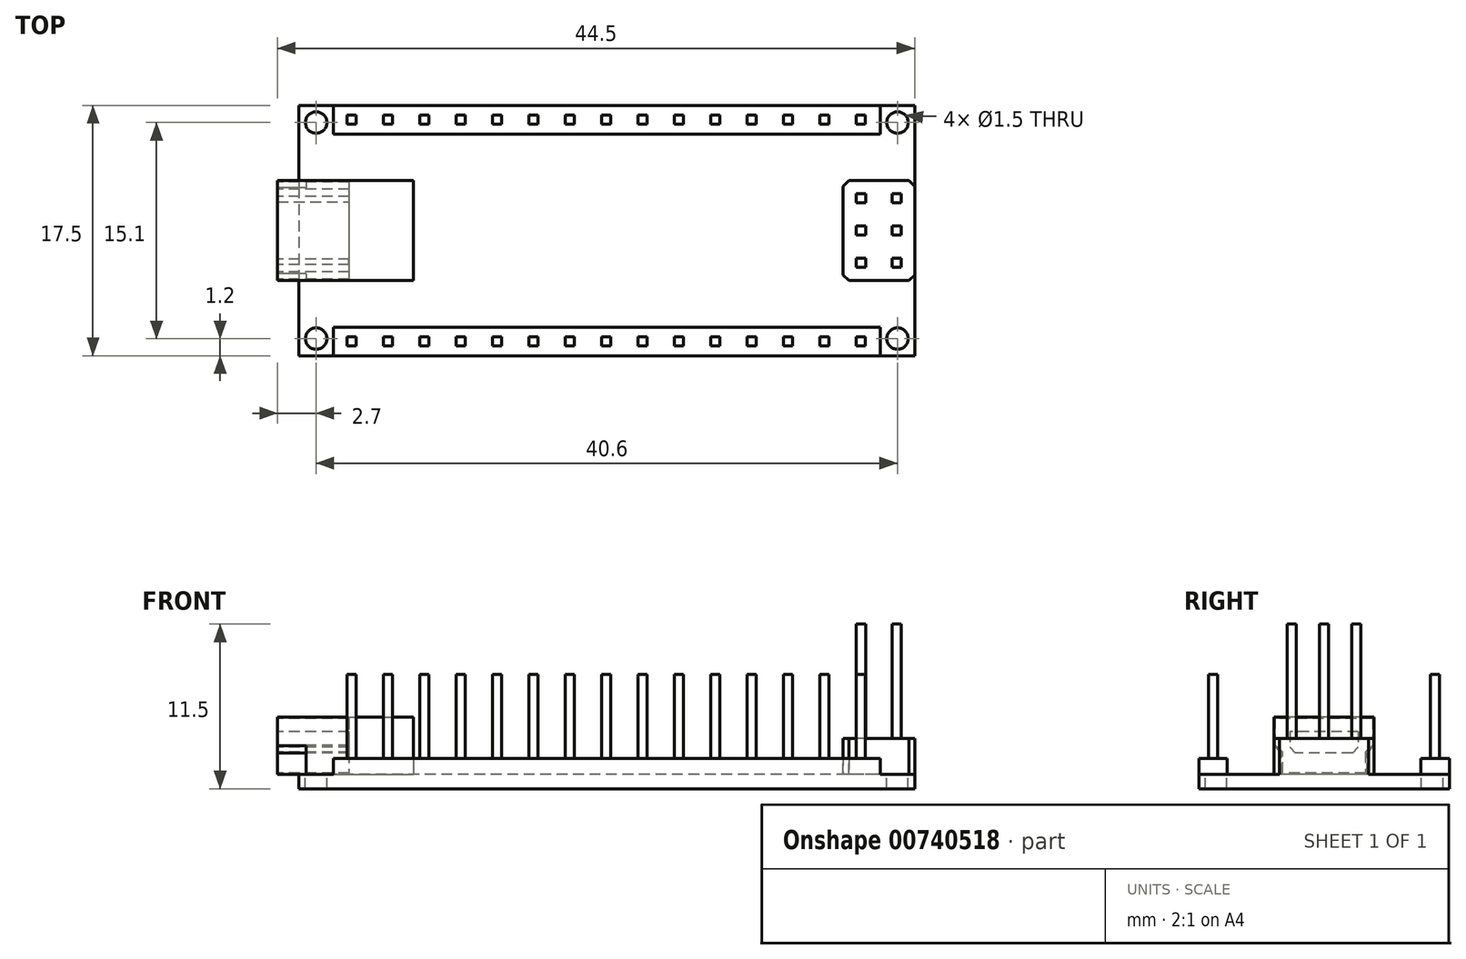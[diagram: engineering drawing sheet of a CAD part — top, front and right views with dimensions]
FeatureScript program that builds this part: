
annotation { "Feature Type Name" : "Feature", "Feature Type Description" : "" }
export const myFeature = defineFeature(function(context is Context, id is Id, definition is map)
    precondition{}
    {
        {
            var Q0;
            Q0=qCreatedBy(makeId("Top.planeOp"),FACE);
            var sketch = newSketch(context, id + "F0", { "sketchPlane" : qUnion([Q0])});
            skLineSegment(sketch, "E0.bottom", {"start": v(21.5, 8.75) * mm, "end": v(-21.5, 8.75) * mm});
            skLineSegment(sketch, "E0.top", {"start": v(21.5, -8.75) * mm, "end": v(-21.5, -8.75) * mm});
            skLineSegment(sketch, "E0.left", {"start": v(21.5, 8.75) * mm, "end": v(21.5, -8.75) * mm});
            skLineSegment(sketch, "E0.right", {"start": v(-21.5, 8.75) * mm, "end": v(-21.5, -8.75) * mm});
            skPoint(sketch, "E0.middle", {"position": v(0, 0) * mm});
            skCircle(sketch, "E1", {"center": v(-20.3, 7.55) * mm, "radius": 0.75 * mm});
            skCircle(sketch, "E2.0.1.0", {"center": v(-20.3, -7.55) * mm, "radius": 0.75 * mm});
            skCircle(sketch, "E2.1.0.0", {"center": v(20.3, 7.55) * mm, "radius": 0.75 * mm});
            skCircle(sketch, "E2.1.1.0", {"center": v(20.3, -7.55) * mm, "radius": 0.75 * mm});
            skLineSegment(sketch, "E2.direction1", {"start": v(-20.3, 7.55) * mm, "end": v(20.3, 7.55) * mm, "construction": true});
            skLineSegment(sketch, "E2.direction2", {"start": v(-20.3, 7.55) * mm, "end": v(-20.3, -7.55) * mm, "construction": true});
            skPoint(sketch, "E3", {"position": v(21.5, 0) * mm});
            skPoint(sketch, "E4", {"position": v(-21.5, 0) * mm});
            skLineSegment(sketch, "E5.bottom", {"start": v(-23, 3.5) * mm, "end": v(-13.5, 3.5) * mm});
            skLineSegment(sketch, "E5.top", {"start": v(-23, -3.5) * mm, "end": v(-13.5, -3.5) * mm});
            skLineSegment(sketch, "E5.left", {"start": v(-23, 3.5) * mm, "end": v(-23, -3.5) * mm});
            skLineSegment(sketch, "E5.right", {"start": v(-13.5, 3.5) * mm, "end": v(-13.5, -3.5) * mm});
            skPoint(sketch, "E6", {"position": v(-13.5, 0) * mm});
            skLineSegment(sketch, "E7.bottom", {"start": v(21.5, 3.5) * mm, "end": v(16.5, 3.5) * mm});
            skLineSegment(sketch, "E7.top", {"start": v(21.5, -3.5) * mm, "end": v(16.5, -3.5) * mm});
            skLineSegment(sketch, "E7.left", {"start": v(21.5, 3.5) * mm, "end": v(21.5, -3.5) * mm});
            skLineSegment(sketch, "E7.right", {"start": v(16.5, 3.5) * mm, "end": v(16.5, -3.5) * mm});
            skSolve(sketch);
        }
        {
            var Q0;
            {var subQ5=sQuery(id+"F0.wireOp",EDGE,"E5.right");Q0=makeQuery(id+"F0.imprint","IMPRINT",FACE,{"disambiguationData":[TD([[makeQuery(id+"F0.imprint","IMPRINT",EDGE,{"derivedFrom":subQ5}),-1.0]])]});}
            var Q1;
            {var subQ1=sQuery(id+"F0.wireOp",EDGE,"E0.bottom");Q1=makeQuery(id+"F0.imprint","IMPRINT",FACE,{"disambiguationData":[TD([[makeQuery(id+"F0.imprint","IMPRINT",EDGE,{"derivedFrom":subQ1}),1.0]])]});}
            var Q2;
            {var subQ0=sQuery(id+"F0.wireOp",EDGE,"E7.bottom");Q2=makeQuery(id+"F0.imprint","IMPRINT",FACE,{"disambiguationData":[TD([[makeQuery(id+"F0.imprint","IMPRINT",EDGE,{"derivedFrom":subQ0}),1.0]])]});}
            extrude(context, id + "F1", {"entities" : qUnion([Q0, Q1, Q2]), "oppositeDirection" : true, "depth" : 1 * mm});
        }
        {
            var Q0;
            {var subQ5=sQuery(id+"F0.wireOp",EDGE,"E5.left");Q0=makeQuery(id+"F0.imprint","IMPRINT",FACE,{"disambiguationData":[TD([[makeQuery(id+"F0.imprint","IMPRINT",EDGE,{"derivedFrom":subQ5}),1.0]])]});}
            var Q1;
            {var subQ5=sQuery(id+"F0.wireOp",EDGE,"E5.right");Q1=makeQuery(id+"F0.imprint","IMPRINT",FACE,{"disambiguationData":[TD([[makeQuery(id+"F0.imprint","IMPRINT",EDGE,{"derivedFrom":subQ5}),-1.0]])]});}
            extrude(context, id + "F2", {"entities" : qUnion([Q0, Q1]), "operationType" : NewBodyOperationType.ADD, "depth" : 4 * mm});
        }
        {
            var Q0;
            {var subQ0=sQuery(id+"F0.wireOp",EDGE,"E7.bottom");Q0=makeQuery(id+"F0.imprint","IMPRINT",FACE,{"disambiguationData":[TD([[makeQuery(id+"F0.imprint","IMPRINT",EDGE,{"derivedFrom":subQ0}),1.0]])]});}
            extrude(context, id + "F3", {"entities" : qUnion([Q0]), "operationType" : NewBodyOperationType.ADD, "depth" : 2.5 * mm});
        }
        {
            var Q0;
            Q0=makeQuery(id+"F2.opExtrude","SWEPT_FACE",FACE,{"disambiguationData":[OSD([sQuery(id+"F0.wireOp",EDGE,"E5.left")])]});
            var sketch = newSketch(context, id + "F4", { "sketchPlane" : qUnion([Q0])});
            skPoint(sketch, "E8", {"position": v(-3.5, 2) * mm});
            skPoint(sketch, "E9", {"position": v(3.5, 2) * mm});
            skPoint(sketch, "E10", {"position": v(-3, 0) * mm});
            skPoint(sketch, "E11", {"position": v(3, 0) * mm});
            skPoint(sketch, "E12", {"position": v(-3, 1.5) * mm});
            skPoint(sketch, "E13", {"position": v(3, 1.5) * mm});
            skLineSegment(sketch, "E14", {"start": v(-3.5, 2) * mm, "end": v(-3, 1.5) * mm});
            skLineSegment(sketch, "E15", {"start": v(-3, 0) * mm, "end": v(-3, 1.5) * mm});
            skLineSegment(sketch, "E16", {"start": v(3, 0) * mm, "end": v(3, 1.5) * mm});
            skLineSegment(sketch, "E17", {"start": v(3, 1.5) * mm, "end": v(3.5, 2) * mm});
            skLineSegment(sketch, "E18.bottom", {"start": v(-2.4, 3) * mm, "end": v(2.4, 3) * mm});
            skLineSegment(sketch, "E18.top", {"start": v(-2.4, 1.5) * mm, "end": v(2.4, 1.5) * mm});
            skLineSegment(sketch, "E18.left", {"start": v(-2.4, 3) * mm, "end": v(-2.4, 1.5) * mm});
            skLineSegment(sketch, "E18.right", {"start": v(2.4, 3) * mm, "end": v(2.4, 1.5) * mm});
            skPoint(sketch, "E19", {"position": v(0, 3) * mm});
            skPoint(sketch, "E20", {"position": v(-2.4, 2.25) * mm});
            skPoint(sketch, "E21", {"position": v(-3.5, 4) * mm});
            skPoint(sketch, "E22", {"position": v(3.5, 4) * mm});
            skLineSegment(sketch, "E23.0", {"start": v(-3.5, -1) * mm, "end": v(3.5, -1) * mm});
            skLineSegment(sketch, "E24", {"start": v(-3.5, 4) * mm, "end": v(-3.5, 2) * mm});
            skLineSegment(sketch, "E25", {"start": v(-3, 1.5) * mm, "end": v(-3, 0) * mm});
            skLineSegment(sketch, "E26", {"start": v(-3, 0) * mm, "end": v(3, 0) * mm});
            skLineSegment(sketch, "E27", {"start": v(3.5, 2) * mm, "end": v(3.5, 4) * mm});
            skLineSegment(sketch, "E28.0", {"start": v(-3.4, 3.9) * mm, "end": v(3.4, 3.9) * mm});
            skLineSegment(sketch, "E28.1", {"start": v(3.4, 2.04) * mm, "end": v(3.4, 3.9) * mm});
            skLineSegment(sketch, "E28.2", {"start": v(-3.4, 3.9) * mm, "end": v(-3.4, 2.04) * mm});
            skLineSegment(sketch, "E28.3", {"start": v(2.9, 1.54) * mm, "end": v(3.4, 2.04) * mm});
            skLineSegment(sketch, "E28.4", {"start": v(-3.4, 2.04) * mm, "end": v(-2.9, 1.54) * mm});
            skLineSegment(sketch, "E28.5", {"start": v(-2.9, 1.54) * mm, "end": v(-2.9, 0.1) * mm});
            skLineSegment(sketch, "E28.6", {"start": v(-2.9, 0.1) * mm, "end": v(2.9, 0.1) * mm});
            skLineSegment(sketch, "E28.7", {"start": v(2.9, 0.1) * mm, "end": v(2.9, 1.54) * mm});
            skPoint(sketch, "E29", {"position": v(-3.4, 2.04) * mm});
            skPoint(sketch, "E30", {"position": v(-2.9, 1.54) * mm});
            skSolve(sketch);
        }
        {
            var Q0;
            Q0=makeQuery(id+"F4.imprint","IMPRINT",FACE,{"disambiguationData":[TD([[makeQuery(id+"F4.imprint","IMPRINT",EDGE,{"derivedFrom":sQuery(id+"F4.wireOp",EDGE,"E18.bottom")}),1.0]])]});
            extrude(context, id + "F5", {"entities" : qUnion([Q0]), "operationType" : NewBodyOperationType.REMOVE, "oppositeDirection" : true, "depth" : 5 * mm});
        }
        {
            var Q0;
            {var subQ0=sQuery(id+"F4.wireOp",EDGE,"E14");Q0=makeQuery(id+"F4.imprint","IMPRINT",FACE,{"disambiguationData":[TD([[makeQuery(id+"F4.imprint","IMPRINT",EDGE,{"derivedFrom":subQ0}),-1.0]])]});}
            var Q1;
            {var subQ0=sQuery(id+"F4.wireOp",EDGE,"E16");Q1=makeQuery(id+"F4.imprint","IMPRINT",FACE,{"disambiguationData":[TD([[makeQuery(id+"F4.imprint","IMPRINT",EDGE,{"derivedFrom":subQ0}),-1.0]])]});}
            extrude(context, id + "F6", {"entities" : qUnion([Q0, Q1]), "operationType" : NewBodyOperationType.REMOVE, "oppositeDirection" : true, "depth" : 2 * mm});
        }
        {
            var Q0;
            Q0=makeQuery(id+"F1.opExtrude","CAP_FACE",FACE,{"disambiguationData":[OSD([sQuery(id+"F0.wireOp",EDGE,"E0.bottom"),sQuery(id+"F0.wireOp",EDGE,"E0.top"),sQuery(id+"F0.wireOp",EDGE,"E0.left"),sQuery(id+"F0.wireOp",EDGE,"E0.right"),sQuery(id+"F0.wireOp",EDGE,"E1"),sQuery(id+"F0.wireOp",EDGE,"E2.0.1.0"),sQuery(id+"F0.wireOp",EDGE,"E2.1.0.0"),sQuery(id+"F0.wireOp",EDGE,"E2.1.1.0")])],"isStart":false});
            var sketch = newSketch(context, id + "F7", { "sketchPlane" : qUnion([Q0])});
            skLineSegment(sketch, "E31.bottom", {"start": v(-19.1, 8.75) * mm, "end": v(19.1, 8.75) * mm});
            skLineSegment(sketch, "E31.top", {"start": v(-19.1, 6.75) * mm, "end": v(19.1, 6.75) * mm});
            skLineSegment(sketch, "E31.left", {"start": v(-19.1, 8.75) * mm, "end": v(-19.1, 6.75) * mm});
            skLineSegment(sketch, "E31.right", {"start": v(19.1, 8.75) * mm, "end": v(19.1, 6.75) * mm});
            skPoint(sketch, "E32", {"position": v(0, 6.75) * mm});
            skLineSegment(sketch, "E33", {"start": v(-19.1, 7.75) * mm, "end": v(19.1, 7.75) * mm, "construction": true});
            skPoint(sketch, "E34", {"position": v(-17.83, 7.75) * mm});
            skLineSegment(sketch, "E35.bottom", {"start": v(-17.51, 8.07) * mm, "end": v(-18.15, 8.07) * mm});
            skLineSegment(sketch, "E35.top", {"start": v(-17.51, 7.43) * mm, "end": v(-18.15, 7.43) * mm});
            skLineSegment(sketch, "E35.left", {"start": v(-17.51, 8.07) * mm, "end": v(-17.51, 7.43) * mm});
            skLineSegment(sketch, "E35.right", {"start": v(-18.15, 8.07) * mm, "end": v(-18.15, 7.43) * mm});
            skPoint(sketch, "E36.1.0.0", {"position": v(-15.3, 7.75) * mm});
            skLineSegment(sketch, "E36.1.0.1", {"start": v(-14.97, 8.07) * mm, "end": v(-14.97, 7.43) * mm});
            skLineSegment(sketch, "E36.1.0.2", {"start": v(-14.97, 8.07) * mm, "end": v(-15.61, 8.07) * mm});
            skLineSegment(sketch, "E36.1.0.3", {"start": v(-15.61, 8.07) * mm, "end": v(-15.61, 7.43) * mm});
            skLineSegment(sketch, "E36.1.0.4", {"start": v(-14.97, 7.43) * mm, "end": v(-15.61, 7.43) * mm});
            skPoint(sketch, "E36.2.0.0", {"position": v(-12.75, 7.75) * mm});
            skLineSegment(sketch, "E36.2.0.1", {"start": v(-12.43, 8.07) * mm, "end": v(-12.43, 7.43) * mm});
            skLineSegment(sketch, "E36.2.0.2", {"start": v(-12.43, 8.07) * mm, "end": v(-13.07, 8.07) * mm});
            skLineSegment(sketch, "E36.2.0.3", {"start": v(-13.07, 8.07) * mm, "end": v(-13.07, 7.43) * mm});
            skLineSegment(sketch, "E36.2.0.4", {"start": v(-12.43, 7.43) * mm, "end": v(-13.07, 7.43) * mm});
            skPoint(sketch, "E36.3.0.0", {"position": v(-10.21, 7.75) * mm});
            skLineSegment(sketch, "E36.3.0.1", {"start": v(-9.89, 8.07) * mm, "end": v(-9.89, 7.43) * mm});
            skLineSegment(sketch, "E36.3.0.2", {"start": v(-9.89, 8.07) * mm, "end": v(-10.53, 8.07) * mm});
            skLineSegment(sketch, "E36.3.0.3", {"start": v(-10.53, 8.07) * mm, "end": v(-10.53, 7.43) * mm});
            skLineSegment(sketch, "E36.3.0.4", {"start": v(-9.89, 7.43) * mm, "end": v(-10.53, 7.43) * mm});
            skPoint(sketch, "E36.4.0.0", {"position": v(-7.67, 7.75) * mm});
            skLineSegment(sketch, "E36.4.0.1", {"start": v(-7.35, 8.07) * mm, "end": v(-7.35, 7.43) * mm});
            skLineSegment(sketch, "E36.4.0.2", {"start": v(-7.35, 8.07) * mm, "end": v(-8, 8.07) * mm});
            skLineSegment(sketch, "E36.4.0.3", {"start": v(-8, 8.07) * mm, "end": v(-8, 7.43) * mm});
            skLineSegment(sketch, "E36.4.0.4", {"start": v(-7.35, 7.43) * mm, "end": v(-8, 7.43) * mm});
            skPoint(sketch, "E36.5.0.0", {"position": v(-5.13, 7.75) * mm});
            skLineSegment(sketch, "E36.5.0.1", {"start": v(-4.8, 8.07) * mm, "end": v(-4.8, 7.43) * mm});
            skLineSegment(sketch, "E36.5.0.2", {"start": v(-4.8, 8.07) * mm, "end": v(-5.45, 8.07) * mm});
            skLineSegment(sketch, "E36.5.0.3", {"start": v(-5.45, 8.07) * mm, "end": v(-5.45, 7.43) * mm});
            skLineSegment(sketch, "E36.5.0.4", {"start": v(-4.8, 7.43) * mm, "end": v(-5.45, 7.43) * mm});
            skPoint(sketch, "E36.6.0.0", {"position": v(-2.59, 7.75) * mm});
            skLineSegment(sketch, "E36.6.0.1", {"start": v(-2.27, 8.07) * mm, "end": v(-2.27, 7.43) * mm});
            skLineSegment(sketch, "E36.6.0.2", {"start": v(-2.27, 8.07) * mm, "end": v(-2.9, 8.07) * mm});
            skLineSegment(sketch, "E36.6.0.3", {"start": v(-2.9, 8.07) * mm, "end": v(-2.9, 7.43) * mm});
            skLineSegment(sketch, "E36.6.0.4", {"start": v(-2.27, 7.43) * mm, "end": v(-2.9, 7.43) * mm});
            skPoint(sketch, "E36.7.0.0", {"position": v(-0.05, 7.75) * mm});
            skLineSegment(sketch, "E36.7.0.1", {"start": v(0.27, 8.07) * mm, "end": v(0.27, 7.43) * mm});
            skLineSegment(sketch, "E36.7.0.2", {"start": v(0.27, 8.07) * mm, "end": v(-0.37, 8.07) * mm});
            skLineSegment(sketch, "E36.7.0.3", {"start": v(-0.37, 8.07) * mm, "end": v(-0.37, 7.43) * mm});
            skLineSegment(sketch, "E36.7.0.4", {"start": v(0.27, 7.43) * mm, "end": v(-0.37, 7.43) * mm});
            skPoint(sketch, "E36.8.0.0", {"position": v(2.5, 7.75) * mm});
            skLineSegment(sketch, "E36.8.0.1", {"start": v(2.81, 8.07) * mm, "end": v(2.81, 7.43) * mm});
            skLineSegment(sketch, "E36.8.0.2", {"start": v(2.81, 8.07) * mm, "end": v(2.17, 8.07) * mm});
            skLineSegment(sketch, "E36.8.0.3", {"start": v(2.17, 8.07) * mm, "end": v(2.17, 7.43) * mm});
            skLineSegment(sketch, "E36.8.0.4", {"start": v(2.81, 7.43) * mm, "end": v(2.17, 7.43) * mm});
            skPoint(sketch, "E36.9.0.0", {"position": v(5.03, 7.75) * mm});
            skLineSegment(sketch, "E36.9.0.1", {"start": v(5.35, 8.07) * mm, "end": v(5.35, 7.43) * mm});
            skLineSegment(sketch, "E36.9.0.2", {"start": v(5.35, 8.07) * mm, "end": v(4.71, 8.07) * mm});
            skLineSegment(sketch, "E36.9.0.3", {"start": v(4.71, 8.07) * mm, "end": v(4.71, 7.43) * mm});
            skLineSegment(sketch, "E36.9.0.4", {"start": v(5.35, 7.43) * mm, "end": v(4.71, 7.43) * mm});
            skPoint(sketch, "E36.10.0.0", {"position": v(7.57, 7.75) * mm});
            skLineSegment(sketch, "E36.10.0.1", {"start": v(7.9, 8.07) * mm, "end": v(7.9, 7.43) * mm});
            skLineSegment(sketch, "E36.10.0.2", {"start": v(7.9, 8.07) * mm, "end": v(7.25, 8.07) * mm});
            skLineSegment(sketch, "E36.10.0.3", {"start": v(7.25, 8.07) * mm, "end": v(7.25, 7.43) * mm});
            skLineSegment(sketch, "E36.10.0.4", {"start": v(7.9, 7.43) * mm, "end": v(7.25, 7.43) * mm});
            skPoint(sketch, "E36.11.0.0", {"position": v(10.11, 7.75) * mm});
            skLineSegment(sketch, "E36.11.0.1", {"start": v(10.43, 8.07) * mm, "end": v(10.43, 7.43) * mm});
            skLineSegment(sketch, "E36.11.0.2", {"start": v(10.43, 8.07) * mm, "end": v(9.8, 8.07) * mm});
            skLineSegment(sketch, "E36.11.0.3", {"start": v(9.8, 8.07) * mm, "end": v(9.8, 7.43) * mm});
            skLineSegment(sketch, "E36.11.0.4", {"start": v(10.43, 7.43) * mm, "end": v(9.8, 7.43) * mm});
            skPoint(sketch, "E36.12.0.0", {"position": v(12.65, 7.75) * mm});
            skLineSegment(sketch, "E36.12.0.1", {"start": v(12.97, 8.07) * mm, "end": v(12.97, 7.43) * mm});
            skLineSegment(sketch, "E36.12.0.2", {"start": v(12.97, 8.07) * mm, "end": v(12.33, 8.07) * mm});
            skLineSegment(sketch, "E36.12.0.3", {"start": v(12.33, 8.07) * mm, "end": v(12.33, 7.43) * mm});
            skLineSegment(sketch, "E36.12.0.4", {"start": v(12.97, 7.43) * mm, "end": v(12.33, 7.43) * mm});
            skPoint(sketch, "E36.13.0.0", {"position": v(15.2, 7.75) * mm});
            skLineSegment(sketch, "E36.13.0.1", {"start": v(15.51, 8.07) * mm, "end": v(15.51, 7.43) * mm});
            skLineSegment(sketch, "E36.13.0.2", {"start": v(15.51, 8.07) * mm, "end": v(14.87, 8.07) * mm});
            skLineSegment(sketch, "E36.13.0.3", {"start": v(14.87, 8.07) * mm, "end": v(14.87, 7.43) * mm});
            skLineSegment(sketch, "E36.13.0.4", {"start": v(15.51, 7.43) * mm, "end": v(14.87, 7.43) * mm});
            skPoint(sketch, "E36.14.0.0", {"position": v(17.73, 7.75) * mm});
            skLineSegment(sketch, "E36.14.0.1", {"start": v(18.05, 8.07) * mm, "end": v(18.05, 7.43) * mm});
            skLineSegment(sketch, "E36.14.0.2", {"start": v(18.05, 8.07) * mm, "end": v(17.41, 8.07) * mm});
            skLineSegment(sketch, "E36.14.0.3", {"start": v(17.41, 8.07) * mm, "end": v(17.41, 7.43) * mm});
            skLineSegment(sketch, "E36.14.0.4", {"start": v(18.05, 7.43) * mm, "end": v(17.41, 7.43) * mm});
            skLineSegment(sketch, "E36.direction1", {"start": v(-17.83, 7.75) * mm, "end": v(-15.3, 7.75) * mm, "construction": true});
            skPoint(sketch, "E37", {"position": v(-20.3, 7.55) * mm});
            skLineSegment(sketch, "E38", {"start": v(-20.3, 7.55) * mm, "end": v(-21.5, 7.55) * mm});
            skLineSegment(sketch, "E39", {"start": v(-21.5, 7.55) * mm, "end": v(-19.1, 7.55) * mm});
            skPoint(sketch, "E40", {"position": v(-21.05, 7.55) * mm});
            skPoint(sketch, "E41", {"position": v(-19.55, 7.55) * mm});
            skPoint(sketch, "E42", {"position": v(20.3, 7.55) * mm});
            skLineSegment(sketch, "E43", {"start": v(20.3, 7.55) * mm, "end": v(21.5, 7.55) * mm});
            skLineSegment(sketch, "E44", {"start": v(21.5, 7.55) * mm, "end": v(19.1, 7.55) * mm});
            skPoint(sketch, "E45", {"position": v(21.05, 7.55) * mm});
            skPoint(sketch, "E46", {"position": v(19.55, 7.55) * mm});
            skPoint(sketch, "E47.0.1.0", {"position": v(-0.05, -7.75) * mm});
            skPoint(sketch, "E47.0.1.1", {"position": v(-5.13, -7.75) * mm});
            skPoint(sketch, "E47.0.1.2", {"position": v(12.65, -7.75) * mm});
            skPoint(sketch, "E47.0.1.3", {"position": v(-7.67, -7.75) * mm});
            skPoint(sketch, "E47.0.1.4", {"position": v(17.73, -7.75) * mm});
            skPoint(sketch, "E47.0.1.5", {"position": v(-10.21, -7.75) * mm});
            skPoint(sketch, "E47.0.1.6", {"position": v(7.57, -7.75) * mm});
            skPoint(sketch, "E47.0.1.7", {"position": v(2.49, -7.75) * mm});
            skPoint(sketch, "E47.0.1.8", {"position": v(0, -8.75) * mm});
            skPoint(sketch, "E47.0.1.9", {"position": v(-17.83, -7.75) * mm});
            skPoint(sketch, "E47.0.1.10", {"position": v(5.03, -7.75) * mm});
            skPoint(sketch, "E47.0.1.11", {"position": v(-15.3, -7.75) * mm});
            skLineSegment(sketch, "E47.0.1.12", {"start": v(-17.83, -7.75) * mm, "end": v(-15.3, -7.75) * mm, "construction": true});
            skPoint(sketch, "E47.0.1.13", {"position": v(10.11, -7.75) * mm});
            skPoint(sketch, "E47.0.1.14", {"position": v(15.2, -7.75) * mm});
            skPoint(sketch, "E47.0.1.15", {"position": v(-2.6, -7.75) * mm});
            skPoint(sketch, "E47.0.1.16", {"position": v(-12.75, -7.75) * mm});
            skPoint(sketch, "E47.0.1.17", {"position": v(-17.83, -7.75) * mm});
            skLineSegment(sketch, "E47.0.1.18", {"start": v(18.05, -7.43) * mm, "end": v(17.41, -7.43) * mm});
            skLineSegment(sketch, "E47.0.1.19", {"start": v(18.05, -8.07) * mm, "end": v(17.41, -8.07) * mm});
            skLineSegment(sketch, "E47.0.1.20", {"start": v(18.05, -7.43) * mm, "end": v(18.05, -8.07) * mm});
            skLineSegment(sketch, "E47.0.1.21", {"start": v(-0.37, -7.43) * mm, "end": v(-0.37, -8.07) * mm});
            skLineSegment(sketch, "E47.0.1.22", {"start": v(-10.53, -7.43) * mm, "end": v(-10.53, -8.07) * mm});
            skLineSegment(sketch, "E47.0.1.23", {"start": v(-9.89, -7.43) * mm, "end": v(-10.53, -7.43) * mm});
            skLineSegment(sketch, "E47.0.1.24", {"start": v(-2.27, -7.43) * mm, "end": v(-2.9, -7.43) * mm});
            skLineSegment(sketch, "E47.0.1.25", {"start": v(12.97, -7.43) * mm, "end": v(12.97, -8.07) * mm});
            skLineSegment(sketch, "E47.0.1.26", {"start": v(-5.45, -7.43) * mm, "end": v(-5.45, -8.07) * mm});
            skLineSegment(sketch, "E47.0.1.27", {"start": v(-7.35, -8.07) * mm, "end": v(-7.99, -8.07) * mm});
            skLineSegment(sketch, "E47.0.1.28", {"start": v(2.81, -8.07) * mm, "end": v(2.17, -8.07) * mm});
            skLineSegment(sketch, "E47.0.1.29", {"start": v(12.97, -8.07) * mm, "end": v(12.33, -8.07) * mm});
            skLineSegment(sketch, "E47.0.1.30", {"start": v(7.9, -8.07) * mm, "end": v(7.25, -8.07) * mm});
            skLineSegment(sketch, "E47.0.1.31", {"start": v(7.25, -7.43) * mm, "end": v(7.25, -8.07) * mm});
            skLineSegment(sketch, "E47.0.1.32", {"start": v(-2.9, -7.43) * mm, "end": v(-2.9, -8.07) * mm});
            skLineSegment(sketch, "E47.0.1.33", {"start": v(-7.35, -7.43) * mm, "end": v(-7.99, -7.43) * mm});
            skLineSegment(sketch, "E47.0.1.34", {"start": v(2.81, -7.43) * mm, "end": v(2.81, -8.07) * mm});
            skLineSegment(sketch, "E47.0.1.35", {"start": v(7.9, -7.43) * mm, "end": v(7.25, -7.43) * mm});
            skLineSegment(sketch, "E47.0.1.36", {"start": v(-4.8, -8.07) * mm, "end": v(-5.45, -8.07) * mm});
            skLineSegment(sketch, "E47.0.1.37", {"start": v(-7.35, -7.43) * mm, "end": v(-7.35, -8.07) * mm});
            skLineSegment(sketch, "E47.0.1.38", {"start": v(15.5, -8.07) * mm, "end": v(14.87, -8.07) * mm});
            skLineSegment(sketch, "E47.0.1.39", {"start": v(5.35, -8.07) * mm, "end": v(4.71, -8.07) * mm});
            skLineSegment(sketch, "E47.0.1.40", {"start": v(-2.27, -8.07) * mm, "end": v(-2.9, -8.07) * mm});
            skLineSegment(sketch, "E47.0.1.41", {"start": v(-12.43, -8.07) * mm, "end": v(-13.07, -8.07) * mm});
            skLineSegment(sketch, "E47.0.1.42", {"start": v(2.81, -7.43) * mm, "end": v(2.17, -7.43) * mm});
            skLineSegment(sketch, "E47.0.1.43", {"start": v(17.41, -7.43) * mm, "end": v(17.41, -8.07) * mm});
            skLineSegment(sketch, "E47.0.1.44", {"start": v(12.97, -7.43) * mm, "end": v(12.33, -7.43) * mm});
            skLineSegment(sketch, "E47.0.1.45", {"start": v(7.9, -7.43) * mm, "end": v(7.9, -8.07) * mm});
            skLineSegment(sketch, "E47.0.1.46", {"start": v(-2.27, -7.43) * mm, "end": v(-2.27, -8.07) * mm});
            skLineSegment(sketch, "E47.0.1.47", {"start": v(-17.5, -8.07) * mm, "end": v(-18.15, -8.07) * mm});
            skLineSegment(sketch, "E47.0.1.48", {"start": v(12.33, -7.43) * mm, "end": v(12.33, -8.07) * mm});
            skLineSegment(sketch, "E47.0.1.49", {"start": v(-14.97, -7.43) * mm, "end": v(-14.97, -8.07) * mm});
            skLineSegment(sketch, "E47.0.1.50", {"start": v(2.17, -7.43) * mm, "end": v(2.17, -8.07) * mm});
            skLineSegment(sketch, "E47.0.1.51", {"start": v(-8, -7.43) * mm, "end": v(-8, -8.07) * mm});
            skLineSegment(sketch, "E47.0.1.52", {"start": v(-14.97, -7.43) * mm, "end": v(-15.6, -7.43) * mm});
            skLineSegment(sketch, "E47.0.1.53", {"start": v(-15.61, -7.43) * mm, "end": v(-15.61, -8.07) * mm});
            skLineSegment(sketch, "E47.0.1.54", {"start": v(-14.97, -8.07) * mm, "end": v(-15.6, -8.07) * mm});
            skLineSegment(sketch, "E47.0.1.55", {"start": v(-9.89, -7.43) * mm, "end": v(-9.89, -8.07) * mm});
            skLineSegment(sketch, "E47.0.1.56", {"start": v(0.27, -7.43) * mm, "end": v(0.27, -8.07) * mm});
            skLineSegment(sketch, "E47.0.1.57", {"start": v(10.43, -7.43) * mm, "end": v(10.43, -8.07) * mm});
            skLineSegment(sketch, "E47.0.1.58", {"start": v(-12.43, -7.43) * mm, "end": v(-12.43, -8.07) * mm});
            skLineSegment(sketch, "E47.0.1.59", {"start": v(10.43, -7.43) * mm, "end": v(9.8, -7.43) * mm});
            skLineSegment(sketch, "E47.0.1.60", {"start": v(0.27, -7.43) * mm, "end": v(-0.37, -7.43) * mm});
            skLineSegment(sketch, "E47.0.1.61", {"start": v(15.51, -7.43) * mm, "end": v(15.51, -8.07) * mm});
            skLineSegment(sketch, "E47.0.1.62", {"start": v(5.35, -7.43) * mm, "end": v(5.35, -8.07) * mm});
            skLineSegment(sketch, "E47.0.1.63", {"start": v(-4.8, -7.43) * mm, "end": v(-4.8, -8.07) * mm});
            skLineSegment(sketch, "E47.0.1.64", {"start": v(15.51, -7.43) * mm, "end": v(14.87, -7.43) * mm});
            skLineSegment(sketch, "E47.0.1.65", {"start": v(5.35, -7.43) * mm, "end": v(4.71, -7.43) * mm});
            skLineSegment(sketch, "E47.0.1.66", {"start": v(-4.8, -7.43) * mm, "end": v(-5.45, -7.43) * mm});
            skLineSegment(sketch, "E47.0.1.67", {"start": v(10.43, -8.07) * mm, "end": v(9.8, -8.07) * mm});
            skLineSegment(sketch, "E47.0.1.68", {"start": v(0.27, -8.07) * mm, "end": v(-0.37, -8.07) * mm});
            skLineSegment(sketch, "E47.0.1.69", {"start": v(-9.9, -8.07) * mm, "end": v(-10.53, -8.07) * mm});
            skLineSegment(sketch, "E47.0.1.70", {"start": v(4.71, -7.43) * mm, "end": v(4.71, -8.07) * mm});
            skLineSegment(sketch, "E47.0.1.71", {"start": v(14.87, -7.43) * mm, "end": v(14.87, -8.07) * mm});
            skLineSegment(sketch, "E47.0.1.72", {"start": v(9.8, -7.43) * mm, "end": v(9.8, -8.07) * mm});
            skLineSegment(sketch, "E47.0.1.73", {"start": v(-12.43, -7.43) * mm, "end": v(-13.07, -7.43) * mm});
            skLineSegment(sketch, "E47.0.1.74", {"start": v(-13.07, -7.43) * mm, "end": v(-13.07, -8.07) * mm});
            skLineSegment(sketch, "E47.0.1.75", {"start": v(-18.15, -7.43) * mm, "end": v(-18.15, -8.07) * mm});
            skLineSegment(sketch, "E47.0.1.76", {"start": v(-17.51, -7.43) * mm, "end": v(-17.51, -8.07) * mm});
            skLineSegment(sketch, "E47.0.1.77", {"start": v(-17.5, -7.43) * mm, "end": v(-18.15, -7.43) * mm});
            skLineSegment(sketch, "E47.0.1.78", {"start": v(19.1, -6.75) * mm, "end": v(19.1, -8.75) * mm});
            skLineSegment(sketch, "E47.0.1.79", {"start": v(-19.1, -8.75) * mm, "end": v(19.1, -8.75) * mm});
            skLineSegment(sketch, "E47.0.1.80", {"start": v(-19.1, -6.75) * mm, "end": v(-19.1, -8.75) * mm});
            skLineSegment(sketch, "E47.0.1.81", {"start": v(-19.1, -6.75) * mm, "end": v(19.1, -6.75) * mm});
            skLineSegment(sketch, "E47.direction1", {"start": v(-0.05, 7.75) * mm, "end": v(24.95, 7.75) * mm, "construction": true});
            skLineSegment(sketch, "E47.direction2", {"start": v(-0.05, 7.75) * mm, "end": v(-0.05, -7.75) * mm, "construction": true});
            skSolve(sketch);
        }
        {
            var Q0;
            Q0=makeQuery(id+"F7.imprint","IMPRINT",FACE,{"disambiguationData":[TD([[makeQuery(id+"F7.imprint","IMPRINT",EDGE,{"derivedFrom":sQuery(id+"F7.wireOp",EDGE,"E47.0.1.18")}),-1.0]])]});
            var Q1;
            {var subQ1=sQuery(id+"F7.wireOp",EDGE,"E31.bottom");Q1=makeQuery(id+"F7.imprint","IMPRINT",FACE,{"disambiguationData":[TD([[makeQuery(id+"F7.imprint","IMPRINT",EDGE,{"derivedFrom":subQ1}),1.0]])]});}
            extrude(context, id + "F8", {"entities" : qUnion([Q0, Q1]), "oppositeDirection" : true, "depth" : 2.1 * mm, "offsetDistance" : 25 * mm});
        }
        {
            var Q0;
            Q0=makeQuery(id+"F7.imprint","IMPRINT",FACE,{"disambiguationData":[TD([[makeQuery(id+"F7.imprint","IMPRINT",EDGE,{"derivedFrom":sQuery(id+"F7.wireOp",EDGE,"E35.bottom")}),1.0]])]});
            var Q1;
            Q1=makeQuery(id+"F7.imprint","IMPRINT",FACE,{"disambiguationData":[TD([[makeQuery(id+"F7.imprint","IMPRINT",EDGE,{"derivedFrom":sQuery(id+"F7.wireOp",EDGE,"E36.1.0.1")}),-1.0]])]});
            var Q2;
            Q2=makeQuery(id+"F7.imprint","IMPRINT",FACE,{"disambiguationData":[TD([[makeQuery(id+"F7.imprint","IMPRINT",EDGE,{"derivedFrom":sQuery(id+"F7.wireOp",EDGE,"E36.2.0.1")}),-1.0]])]});
            var Q3;
            Q3=makeQuery(id+"F7.imprint","IMPRINT",FACE,{"disambiguationData":[TD([[makeQuery(id+"F7.imprint","IMPRINT",EDGE,{"derivedFrom":sQuery(id+"F7.wireOp",EDGE,"E36.3.0.1")}),-1.0]])]});
            var Q4;
            Q4=makeQuery(id+"F7.imprint","IMPRINT",FACE,{"disambiguationData":[TD([[makeQuery(id+"F7.imprint","IMPRINT",EDGE,{"derivedFrom":sQuery(id+"F7.wireOp",EDGE,"E36.4.0.1")}),-1.0]])]});
            var Q5;
            Q5=makeQuery(id+"F7.imprint","IMPRINT",FACE,{"disambiguationData":[TD([[makeQuery(id+"F7.imprint","IMPRINT",EDGE,{"derivedFrom":sQuery(id+"F7.wireOp",EDGE,"E36.5.0.1")}),-1.0]])]});
            var Q6;
            Q6=makeQuery(id+"F7.imprint","IMPRINT",FACE,{"disambiguationData":[TD([[makeQuery(id+"F7.imprint","IMPRINT",EDGE,{"derivedFrom":sQuery(id+"F7.wireOp",EDGE,"E36.6.0.1")}),-1.0]])]});
            var Q7;
            Q7=makeQuery(id+"F7.imprint","IMPRINT",FACE,{"disambiguationData":[TD([[makeQuery(id+"F7.imprint","IMPRINT",EDGE,{"derivedFrom":sQuery(id+"F7.wireOp",EDGE,"E36.7.0.1")}),-1.0]])]});
            var Q8;
            Q8=makeQuery(id+"F7.imprint","IMPRINT",FACE,{"disambiguationData":[TD([[makeQuery(id+"F7.imprint","IMPRINT",EDGE,{"derivedFrom":sQuery(id+"F7.wireOp",EDGE,"E36.8.0.1")}),-1.0]])]});
            var Q9;
            Q9=makeQuery(id+"F7.imprint","IMPRINT",FACE,{"disambiguationData":[TD([[makeQuery(id+"F7.imprint","IMPRINT",EDGE,{"derivedFrom":sQuery(id+"F7.wireOp",EDGE,"E36.9.0.1")}),-1.0]])]});
            var Q10;
            Q10=makeQuery(id+"F7.imprint","IMPRINT",FACE,{"disambiguationData":[TD([[makeQuery(id+"F7.imprint","IMPRINT",EDGE,{"derivedFrom":sQuery(id+"F7.wireOp",EDGE,"E36.10.0.1")}),-1.0]])]});
            var Q11;
            Q11=makeQuery(id+"F7.imprint","IMPRINT",FACE,{"disambiguationData":[TD([[makeQuery(id+"F7.imprint","IMPRINT",EDGE,{"derivedFrom":sQuery(id+"F7.wireOp",EDGE,"E36.11.0.1")}),-1.0]])]});
            var Q12;
            Q12=makeQuery(id+"F7.imprint","IMPRINT",FACE,{"disambiguationData":[TD([[makeQuery(id+"F7.imprint","IMPRINT",EDGE,{"derivedFrom":sQuery(id+"F7.wireOp",EDGE,"E36.12.0.1")}),-1.0]])]});
            var Q13;
            Q13=makeQuery(id+"F7.imprint","IMPRINT",FACE,{"disambiguationData":[TD([[makeQuery(id+"F7.imprint","IMPRINT",EDGE,{"derivedFrom":sQuery(id+"F7.wireOp",EDGE,"E36.13.0.1")}),-1.0]])]});
            var Q14;
            Q14=makeQuery(id+"F7.imprint","IMPRINT",FACE,{"disambiguationData":[TD([[makeQuery(id+"F7.imprint","IMPRINT",EDGE,{"derivedFrom":sQuery(id+"F7.wireOp",EDGE,"E36.14.0.1")}),-1.0]])]});
            var Q15;
            Q15=makeQuery(id+"F7.imprint","IMPRINT",FACE,{"disambiguationData":[TD([[makeQuery(id+"F7.imprint","IMPRINT",EDGE,{"derivedFrom":sQuery(id+"F7.wireOp",EDGE,"E47.0.1.47")}),-1.0]])]});
            var Q16;
            Q16=makeQuery(id+"F7.imprint","IMPRINT",FACE,{"disambiguationData":[TD([[makeQuery(id+"F7.imprint","IMPRINT",EDGE,{"derivedFrom":sQuery(id+"F7.wireOp",EDGE,"E47.0.1.49")}),-1.0]])]});
            var Q17;
            Q17=makeQuery(id+"F7.imprint","IMPRINT",FACE,{"disambiguationData":[TD([[makeQuery(id+"F7.imprint","IMPRINT",EDGE,{"derivedFrom":sQuery(id+"F7.wireOp",EDGE,"E47.0.1.41")}),-1.0]])]});
            var Q18;
            Q18=makeQuery(id+"F7.imprint","IMPRINT",FACE,{"disambiguationData":[TD([[makeQuery(id+"F7.imprint","IMPRINT",EDGE,{"derivedFrom":sQuery(id+"F7.wireOp",EDGE,"E47.0.1.22")}),1.0]])]});
            var Q19;
            Q19=makeQuery(id+"F7.imprint","IMPRINT",FACE,{"disambiguationData":[TD([[makeQuery(id+"F7.imprint","IMPRINT",EDGE,{"derivedFrom":sQuery(id+"F7.wireOp",EDGE,"E47.0.1.27")}),-1.0]])]});
            var Q20;
            Q20=makeQuery(id+"F7.imprint","IMPRINT",FACE,{"disambiguationData":[TD([[makeQuery(id+"F7.imprint","IMPRINT",EDGE,{"derivedFrom":sQuery(id+"F7.wireOp",EDGE,"E47.0.1.26")}),1.0]])]});
            var Q21;
            Q21=makeQuery(id+"F7.imprint","IMPRINT",FACE,{"disambiguationData":[TD([[makeQuery(id+"F7.imprint","IMPRINT",EDGE,{"derivedFrom":sQuery(id+"F7.wireOp",EDGE,"E47.0.1.24")}),1.0]])]});
            var Q22;
            Q22=makeQuery(id+"F7.imprint","IMPRINT",FACE,{"disambiguationData":[TD([[makeQuery(id+"F7.imprint","IMPRINT",EDGE,{"derivedFrom":sQuery(id+"F7.wireOp",EDGE,"E47.0.1.21")}),1.0]])]});
            var Q23;
            Q23=makeQuery(id+"F7.imprint","IMPRINT",FACE,{"disambiguationData":[TD([[makeQuery(id+"F7.imprint","IMPRINT",EDGE,{"derivedFrom":sQuery(id+"F7.wireOp",EDGE,"E47.0.1.28")}),-1.0]])]});
            var Q24;
            Q24=makeQuery(id+"F7.imprint","IMPRINT",FACE,{"disambiguationData":[TD([[makeQuery(id+"F7.imprint","IMPRINT",EDGE,{"derivedFrom":sQuery(id+"F7.wireOp",EDGE,"E47.0.1.39")}),-1.0]])]});
            var Q25;
            Q25=makeQuery(id+"F7.imprint","IMPRINT",FACE,{"disambiguationData":[TD([[makeQuery(id+"F7.imprint","IMPRINT",EDGE,{"derivedFrom":sQuery(id+"F7.wireOp",EDGE,"E47.0.1.30")}),-1.0]])]});
            var Q26;
            Q26=makeQuery(id+"F7.imprint","IMPRINT",FACE,{"disambiguationData":[TD([[makeQuery(id+"F7.imprint","IMPRINT",EDGE,{"derivedFrom":sQuery(id+"F7.wireOp",EDGE,"E47.0.1.57")}),-1.0]])]});
            var Q27;
            Q27=makeQuery(id+"F7.imprint","IMPRINT",FACE,{"disambiguationData":[TD([[makeQuery(id+"F7.imprint","IMPRINT",EDGE,{"derivedFrom":sQuery(id+"F7.wireOp",EDGE,"E47.0.1.25")}),-1.0]])]});
            var Q28;
            Q28=makeQuery(id+"F7.imprint","IMPRINT",FACE,{"disambiguationData":[TD([[makeQuery(id+"F7.imprint","IMPRINT",EDGE,{"derivedFrom":sQuery(id+"F7.wireOp",EDGE,"E47.0.1.38")}),-1.0]])]});
            var Q29;
            Q29=makeQuery(id+"F7.imprint","IMPRINT",FACE,{"disambiguationData":[TD([[makeQuery(id+"F7.imprint","IMPRINT",EDGE,{"derivedFrom":sQuery(id+"F7.wireOp",EDGE,"E47.0.1.18")}),1.0]])]});
            extrude(context, id + "F9", {"entities" : qUnion([Q0, Q1, Q2, Q3, Q4, Q5, Q6, Q7, Q8, Q9, Q10, Q11, Q12, Q13, Q14, Q15, Q16, Q17, Q18, Q19, Q20, Q21, Q22, Q23, Q24, Q25, Q26, Q27, Q28, Q29]), "operationType" : NewBodyOperationType.ADD, "oppositeDirection" : true, "depth" : 8 * mm, "offsetDistance" : 25 * mm});
        }
        {
            var Q0;
            Q0=makeQuery(id+"F5.boolean.opBoolean","COPY",EDGE,{"derivedFrom":makeQuery(id+"F5.opExtrude","SWEPT_EDGE",EDGE,{"disambiguationData":[OSD([sQuery(id+"F4.wireOp",EDGE,"E18.top"),sQuery(id+"F4.wireOp",EDGE,"E18.right")])]})});
            var Q1;
            Q1=makeQuery(id+"F5.boolean.opBoolean","COPY",EDGE,{"derivedFrom":makeQuery(id+"F5.opExtrude","SWEPT_EDGE",EDGE,{"disambiguationData":[OSD([sQuery(id+"F4.wireOp",EDGE,"E18.top"),sQuery(id+"F4.wireOp",EDGE,"E18.left")])]})});
            chamfer(context, id + "F10", {"entities" : qUnion([Q0, Q1]), "width" : 0.4 * mm, "tangentPropagation" : true});
        }
        {
            var Q0;
            Q0=makeQuery(id+"F3.opExtrude","CAP_FACE",FACE,{"disambiguationData":[OSD([sQuery(id+"F0.wireOp",EDGE,"E0.left"),sQuery(id+"F0.wireOp",EDGE,"E7.bottom"),sQuery(id+"F0.wireOp",EDGE,"E7.top"),sQuery(id+"F0.wireOp",EDGE,"E7.right")])],"isStart":false});
            var sketch = newSketch(context, id + "F11", { "sketchPlane" : qUnion([Q0])});
            skPoint(sketch, "E48", {"position": v(21.5, 1.17) * mm});
            skPoint(sketch, "E49", {"position": v(21.5, -1.17) * mm});
            skLineSegment(sketch, "E50", {"start": v(21.5, 3.5) * mm, "end": v(21.5, 1.17) * mm});
            skLineSegment(sketch, "E51", {"start": v(21.5, -1.17) * mm, "end": v(21.5, 1.17) * mm});
            skLineSegment(sketch, "E52", {"start": v(21.5, -1.17) * mm, "end": v(21.5, -3.5) * mm});
            skLineSegment(sketch, "E53", {"start": v(21.5, 1.17) * mm, "end": v(16.5, 1.17) * mm});
            skLineSegment(sketch, "E54", {"start": v(21.5, -1.17) * mm, "end": v(16.5, -1.17) * mm});
            skPoint(sketch, "E55", {"position": v(19, 3.5) * mm});
            skPoint(sketch, "E56", {"position": v(19, -3.5) * mm});
            skLineSegment(sketch, "E57", {"start": v(19, 3.5) * mm, "end": v(19, -3.5) * mm});
            skPoint(sketch, "E58", {"position": v(17.75, 2.25) * mm});
            skLineSegment(sketch, "E59", {"start": v(17.75, 2.25) * mm, "end": v(17.75, 3.5) * mm, "construction": true});
            skLineSegment(sketch, "E60", {"start": v(17.75, 2.25) * mm, "end": v(16.5, 2.25) * mm, "construction": true});
            skLineSegment(sketch, "E61", {"start": v(17.75, 2.25) * mm, "end": v(19, 2.25) * mm, "construction": true});
            skLineSegment(sketch, "E62", {"start": v(17.75, 2.25) * mm, "end": v(17.75, 1.17) * mm, "construction": true});
            skLineSegment(sketch, "E63.bottom", {"start": v(18.07, 2.57) * mm, "end": v(17.43, 2.57) * mm});
            skLineSegment(sketch, "E63.top", {"start": v(18.07, 1.93) * mm, "end": v(17.43, 1.93) * mm});
            skLineSegment(sketch, "E63.left", {"start": v(18.07, 2.57) * mm, "end": v(18.07, 1.93) * mm});
            skLineSegment(sketch, "E63.right", {"start": v(17.43, 2.57) * mm, "end": v(17.43, 1.93) * mm});
            skLineSegment(sketch, "E64.1.0.0", {"start": v(20.57, 2.57) * mm, "end": v(20.57, 1.93) * mm});
            skLineSegment(sketch, "E64.1.0.1", {"start": v(20.57, 2.57) * mm, "end": v(19.93, 2.57) * mm});
            skLineSegment(sketch, "E64.1.0.2", {"start": v(19.93, 2.57) * mm, "end": v(19.93, 1.93) * mm});
            skLineSegment(sketch, "E64.1.0.3", {"start": v(20.57, 1.93) * mm, "end": v(19.93, 1.93) * mm});
            skPoint(sketch, "E65", {"position": v(20.25, 2.25) * mm});
            skLineSegment(sketch, "E66", {"start": v(19, 2.25) * mm, "end": v(20.25, 2.25) * mm, "construction": true});
            skLineSegment(sketch, "E67", {"start": v(20.25, 2.25) * mm, "end": v(21.5, 2.25) * mm, "construction": true});
            skLineSegment(sketch, "E68", {"start": v(20.25, 3.5) * mm, "end": v(20.25, 2.25) * mm, "construction": true});
            skPoint(sketch, "E68.startSnap0", {"position": v(20.25, 2.57) * mm});
            skLineSegment(sketch, "E69", {"start": v(20.25, 1.17) * mm, "end": v(20.25, 2.25) * mm, "construction": true});
            skPoint(sketch, "E70", {"position": v(21.5, 0) * mm});
            skPoint(sketch, "E71.0.1.0", {"position": v(20.25, 0) * mm});
            skLineSegment(sketch, "E71.0.1.1", {"start": v(20.57, 0.32) * mm, "end": v(20.57, -0.32) * mm});
            skLineSegment(sketch, "E71.0.1.2", {"start": v(20.57, 0.32) * mm, "end": v(19.93, 0.32) * mm});
            skLineSegment(sketch, "E71.0.1.3", {"start": v(19.93, 0.32) * mm, "end": v(19.93, -0.32) * mm});
            skLineSegment(sketch, "E71.0.1.4", {"start": v(20.57, -0.32) * mm, "end": v(19.93, -0.32) * mm});
            skLineSegment(sketch, "E71.0.1.5", {"start": v(18.07, 0.32) * mm, "end": v(18.07, -0.32) * mm});
            skLineSegment(sketch, "E71.0.1.6", {"start": v(18.07, -0.32) * mm, "end": v(17.43, -0.32) * mm});
            skLineSegment(sketch, "E71.0.1.7", {"start": v(17.43, 0.32) * mm, "end": v(17.43, -0.32) * mm});
            skLineSegment(sketch, "E71.0.1.8", {"start": v(18.07, 0.32) * mm, "end": v(17.43, 0.32) * mm});
            skPoint(sketch, "E71.0.2.0", {"position": v(20.25, -2.25) * mm});
            skLineSegment(sketch, "E71.0.2.1", {"start": v(20.57, -1.93) * mm, "end": v(20.57, -2.57) * mm});
            skLineSegment(sketch, "E71.0.2.2", {"start": v(20.57, -1.93) * mm, "end": v(19.93, -1.93) * mm});
            skLineSegment(sketch, "E71.0.2.3", {"start": v(19.93, -1.93) * mm, "end": v(19.93, -2.57) * mm});
            skLineSegment(sketch, "E71.0.2.4", {"start": v(20.57, -2.57) * mm, "end": v(19.93, -2.57) * mm});
            skLineSegment(sketch, "E71.0.2.5", {"start": v(18.07, -1.93) * mm, "end": v(18.07, -2.57) * mm});
            skLineSegment(sketch, "E71.0.2.6", {"start": v(18.07, -2.57) * mm, "end": v(17.43, -2.57) * mm});
            skLineSegment(sketch, "E71.0.2.7", {"start": v(17.43, -1.93) * mm, "end": v(17.43, -2.57) * mm});
            skLineSegment(sketch, "E71.0.2.8", {"start": v(18.07, -1.93) * mm, "end": v(17.43, -1.93) * mm});
            skLineSegment(sketch, "E71.direction1", {"start": v(20.25, 2.25) * mm, "end": v(31.55, 2.25) * mm, "construction": true});
            skLineSegment(sketch, "E71.direction2", {"start": v(20.25, 2.25) * mm, "end": v(20.25, 0) * mm, "construction": true});
            skSolve(sketch);
        }
        {
            var Q0;
            Q0=makeQuery(id+"F11.imprint","IMPRINT",FACE,{"disambiguationData":[TD([[makeQuery(id+"F11.imprint","IMPRINT",EDGE,{"derivedFrom":sQuery(id+"F11.wireOp",EDGE,"E71.0.2.1")}),-1.0]])]});
            var Q1;
            Q1=makeQuery(id+"F11.imprint","IMPRINT",FACE,{"disambiguationData":[TD([[makeQuery(id+"F11.imprint","IMPRINT",EDGE,{"derivedFrom":sQuery(id+"F11.wireOp",EDGE,"E71.0.2.5")}),-1.0]])]});
            var Q2;
            Q2=makeQuery(id+"F11.imprint","IMPRINT",FACE,{"disambiguationData":[TD([[makeQuery(id+"F11.imprint","IMPRINT",EDGE,{"derivedFrom":sQuery(id+"F11.wireOp",EDGE,"E71.0.1.5")}),-1.0]])]});
            var Q3;
            Q3=makeQuery(id+"F11.imprint","IMPRINT",FACE,{"disambiguationData":[TD([[makeQuery(id+"F11.imprint","IMPRINT",EDGE,{"derivedFrom":sQuery(id+"F11.wireOp",EDGE,"E71.0.1.1")}),-1.0]])]});
            var Q4;
            Q4=makeQuery(id+"F11.imprint","IMPRINT",FACE,{"disambiguationData":[TD([[makeQuery(id+"F11.imprint","IMPRINT",EDGE,{"derivedFrom":sQuery(id+"F11.wireOp",EDGE,"E64.1.0.0")}),-1.0]])]});
            var Q5;
            Q5=makeQuery(id+"F11.imprint","IMPRINT",FACE,{"disambiguationData":[TD([[makeQuery(id+"F11.imprint","IMPRINT",EDGE,{"derivedFrom":sQuery(id+"F11.wireOp",EDGE,"E63.bottom")}),1.0]])]});
            extrude(context, id + "F12", {"entities" : qUnion([Q0, Q1, Q2, Q3, Q4, Q5]), "operationType" : NewBodyOperationType.ADD, "depth" : 8 * mm});
        }
        {
            var Q0;
            Q0=makeQuery(id+"F3.opExtrude","SWEPT_EDGE",EDGE,{"disambiguationData":[OSD([sQuery(id+"F0.wireOp",EDGE,"E0.left"),sQuery(id+"F0.wireOp",EDGE,"E7.bottom")])]});
            var Q1;
            Q1=makeQuery(id+"F3.opExtrude","SWEPT_EDGE",EDGE,{"disambiguationData":[OSD([sQuery(id+"F0.wireOp",EDGE,"E7.bottom"),sQuery(id+"F0.wireOp",EDGE,"E7.right")])]});
            var Q2;
            Q2=makeQuery(id+"F3.opExtrude","SWEPT_EDGE",EDGE,{"disambiguationData":[OSD([sQuery(id+"F0.wireOp",EDGE,"E0.left"),sQuery(id+"F0.wireOp",EDGE,"E7.top")])]});
            var Q3;
            Q3=makeQuery(id+"F3.opExtrude","SWEPT_EDGE",EDGE,{"disambiguationData":[OSD([sQuery(id+"F0.wireOp",EDGE,"E7.top"),sQuery(id+"F0.wireOp",EDGE,"E7.right")])]});
            chamfer(context, id + "F13", {"entities" : qUnion([Q0, Q1, Q2, Q3]), "width" : 0.4 * mm, "tangentPropagation" : true});
        }
    });
